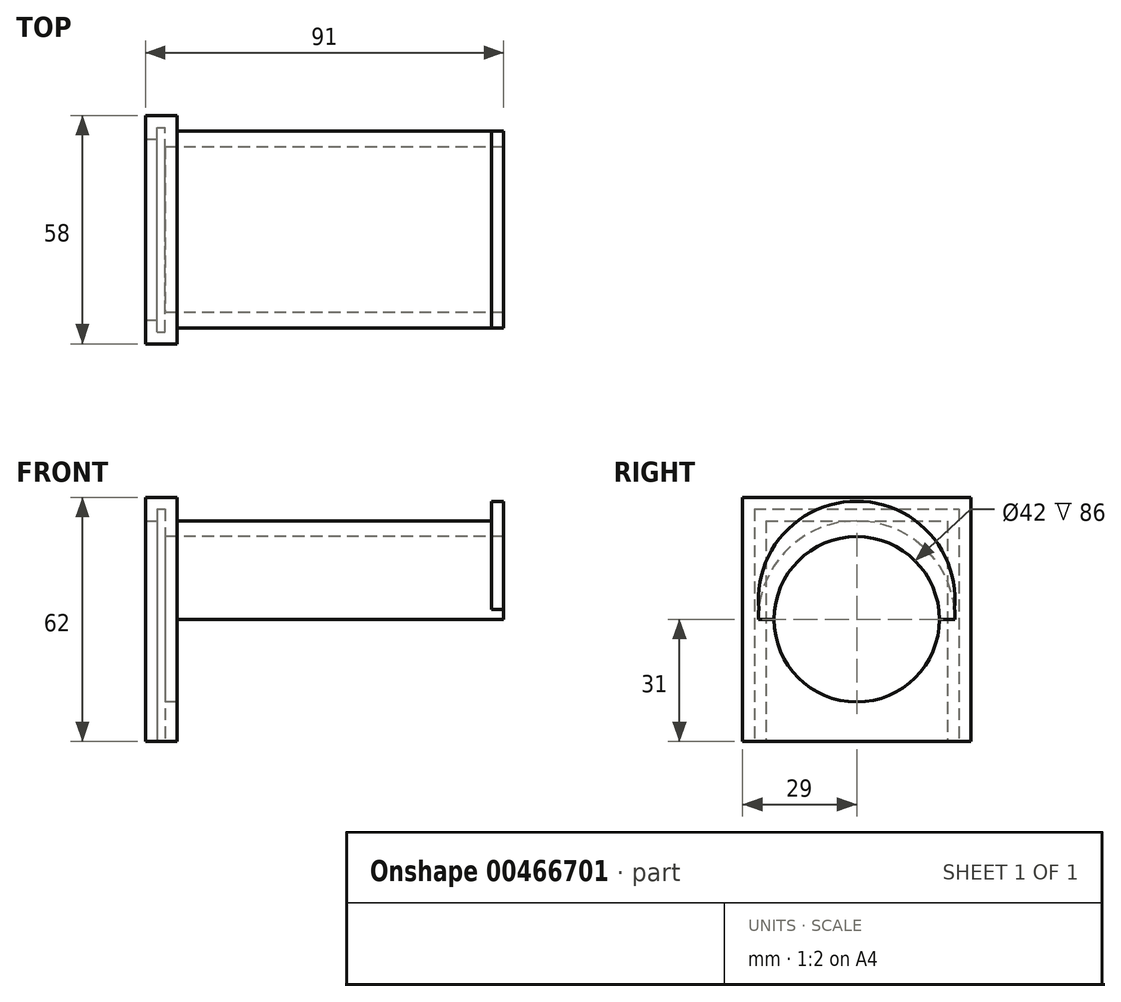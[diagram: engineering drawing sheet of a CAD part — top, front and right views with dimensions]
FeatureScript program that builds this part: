
annotation { "Feature Type Name" : "Feature", "Feature Type Description" : "" }
export const myFeature = defineFeature(function(context is Context, id is Id, definition is map)
    precondition{}
    {
        {
            var Q0;
            Q0=qCreatedBy(makeId("Right.planeOp"),FACE);
            var sketch = newSketch(context, id + "F0", { "sketchPlane" : qUnion([Q0])});
            skLineSegment(sketch, "E0.bottom", {"start": v(-29, 31) * mm, "end": v(29, 31) * mm});
            skLineSegment(sketch, "E0.top", {"start": v(-29, -31) * mm, "end": v(29, -31) * mm});
            skLineSegment(sketch, "E0.left", {"start": v(-29, 31) * mm, "end": v(-29, -31) * mm});
            skLineSegment(sketch, "E0.right", {"start": v(29, 31) * mm, "end": v(29, -31) * mm});
            skCircle(sketch, "E1", {"center": v(0, 0) * mm, "radius": 25 * mm});
            skPoint(sketch, "E2", {"position": v(0, 31) * mm});
            skCircle(sketch, "E3", {"center": v(0, 0) * mm, "radius": 21 * mm});
            skLineSegment(sketch, "E4", {"start": v(-25, 0) * mm, "end": v(-21, 0) * mm});
            skLineSegment(sketch, "E5.trimOffspring", {"start": v(21, 0) * mm, "end": v(25, 0) * mm});
            skSolve(sketch);
        }
        {
            var Q0;
            {var subQ0=sQuery(id+"F0.wireOp",EDGE,"E4");Q0=makeQuery(id+"F0.imprint","IMPRINT",FACE,{"disambiguationData":[TD([[makeQuery(id+"F0.imprint","IMPRINT",EDGE,{"derivedFrom":subQ0}),1.0]])]});}
            extrude(context, id + "F1", {"entities" : qUnion([Q0]), "depth" : 80 * mm});
        }
        {
            var Q0;
            Q0=makeQuery(id+"F0.imprint","IMPRINT",FACE,{"disambiguationData":[TD([[makeQuery(id+"F0.imprint","IMPRINT",EDGE,{"derivedFrom":sQuery(id+"F0.wireOp",EDGE,"E1")}),-1.0]])]});
            var Q1;
            Q1=makeQuery(id+"F0.imprint","IMPRINT",FACE,{"disambiguationData":[TD([[makeQuery(id+"F0.imprint","IMPRINT",EDGE,{"derivedFrom":sQuery(id+"F0.wireOp",EDGE,"E0.bottom")}),-1.0]])]});
            var Q2;
            Q2=makeQuery(id+"F0.imprint","IMPRINT",FACE,{"disambiguationData":[TD([[makeQuery(id+"F0.imprint","IMPRINT",EDGE,{"derivedFrom":sQuery(id+"F0.wireOp",EDGE,"E1")}),1.0]])]});
            extrude(context, id + "F2", {"entities" : qUnion([Q0, Q1, Q2]), "operationType" : NewBodyOperationType.ADD, "oppositeDirection" : true, "depth" : 8 * mm});
        }
        {
            var Q0;
            Q0=makeQuery(id+"F2.opExtrude","SWEPT_FACE",FACE,{"disambiguationData":[OSD([sQuery(id+"F0.wireOp",EDGE,"E0.top")])]});
            var sketch = newSketch(context, id + "F3", { "sketchPlane" : qUnion([Q0])});
            skLineSegment(sketch, "E6.0", {"start": v(-8, 29) * mm, "end": v(-8, -29) * mm});
            skLineSegment(sketch, "E6.1", {"start": v(0, 29) * mm, "end": v(0, -29) * mm});
            skLineSegment(sketch, "E6.2", {"start": v(-8, 29) * mm, "end": v(0, 29) * mm});
            skLineSegment(sketch, "E6.3", {"start": v(-8, -29) * mm, "end": v(0, -29) * mm});
            skLineSegment(sketch, "E7.bottom", {"start": v(-5, 26) * mm, "end": v(-3, 26) * mm});
            skLineSegment(sketch, "E7.top", {"start": v(-5, -26) * mm, "end": v(-3, -26) * mm});
            skLineSegment(sketch, "E7.left", {"start": v(-5, 26) * mm, "end": v(-5, -26) * mm});
            skLineSegment(sketch, "E7.right", {"start": v(-3, 26) * mm, "end": v(-3, -26) * mm});
            skPoint(sketch, "E8", {"position": v(-3, 0) * mm});
            skLineSegment(sketch, "E9.bottom", {"start": v(-8, -23) * mm, "end": v(-5, -23) * mm});
            skLineSegment(sketch, "E9.top", {"start": v(-8, 23) * mm, "end": v(-5, 23) * mm});
            skLineSegment(sketch, "E9.left", {"start": v(-8, -23) * mm, "end": v(-8, 23) * mm});
            skLineSegment(sketch, "E9.right", {"start": v(-5, -23) * mm, "end": v(-5, 23) * mm});
            skSolve(sketch);
        }
        {
            var Q0;
            Q0=makeQuery(id+"F3.imprint","IMPRINT",FACE,{"disambiguationData":[TD([[makeQuery(id+"F3.imprint","IMPRINT",EDGE,{"derivedFrom":sQuery(id+"F3.wireOp",EDGE,"E7.bottom")}),-1.0]])]});
            extrude(context, id + "F4", {"entities" : qUnion([Q0]), "operationType" : NewBodyOperationType.REMOVE, "oppositeDirection" : true, "depth" : 59 * mm});
        }
        {
            var Q0;
            Q0=makeQuery(id+"F3.imprint","IMPRINT",FACE,{"disambiguationData":[TD([[makeQuery(id+"F3.imprint","IMPRINT",EDGE,{"derivedFrom":sQuery(id+"F3.wireOp",EDGE,"E9.bottom")}),1.0]])]});
            extrude(context, id + "F5", {"entities" : qUnion([Q0]), "operationType" : NewBodyOperationType.REMOVE, "oppositeDirection" : true, "depth" : 56 * mm});
        }
        {
            var Q0;
            Q0=makeQuery(id+"F1.opExtrude","CAP_FACE",FACE,{"disambiguationData":[OSD([sQuery(id+"F0.wireOp",EDGE,"E1")])],"isStart":false});
            var sketch = newSketch(context, id + "F6", { "sketchPlane" : qUnion([Q0])});
            skArc(sketch, "E10.0", {"start": v(-24.87, 2.5) * mm, "mid": v(-24.97, 1.25) * mm, "end": v(-25, 0) * mm});
            skArc(sketch, "E11", {"start": v(24.87, 2.5) * mm, "mid": v(0, 30) * mm, "end": v(-24.87, 2.5) * mm});
            skArc(sketch, "E12.0", {"start": v(21, 0) * mm, "mid": v(0, 21) * mm, "end": v(-21, 0) * mm});
            skLineSegment(sketch, "E13.0", {"start": v(-25, 0) * mm, "end": v(-21, 0) * mm});
            skLineSegment(sketch, "E14.0", {"start": v(21, 0) * mm, "end": v(25, 0) * mm});
            skArc(sketch, "E15.trimOffspring", {"start": v(25, 0) * mm, "mid": v(24.97, 1.25) * mm, "end": v(24.87, 2.5) * mm});
            skSolve(sketch);
        }
        {
            var Q0;
            Q0 = qSketchRegion(id + "F6", true);
            extrude(context, id + "F7", {"entities" : qUnion([Q0]), "operationType" : NewBodyOperationType.ADD, "depth" : 3 * mm});
        }
    });
